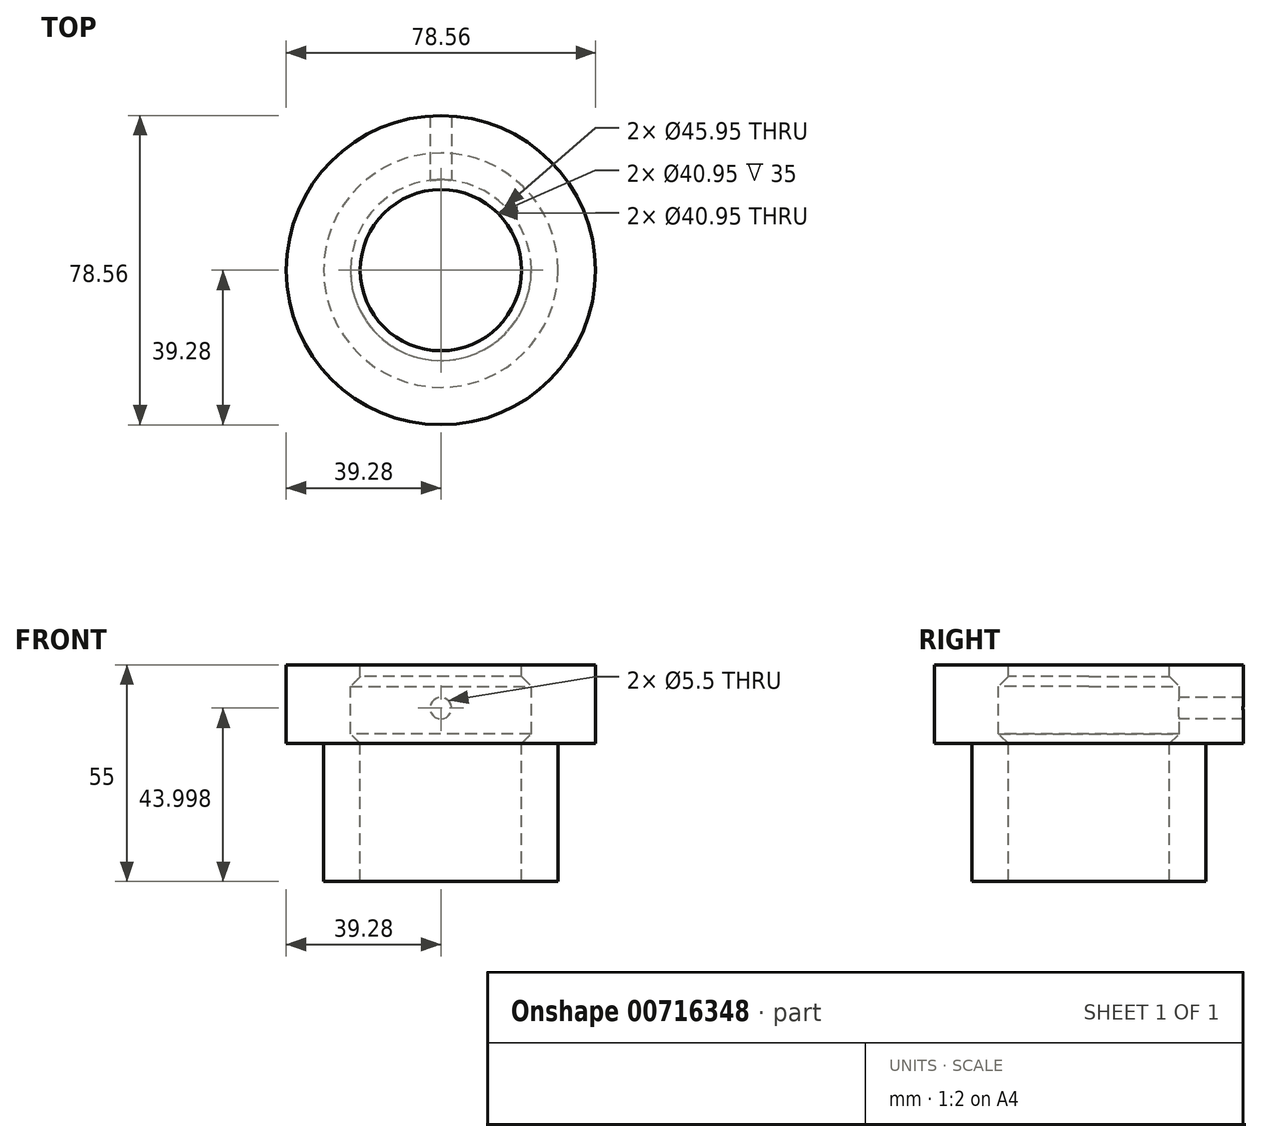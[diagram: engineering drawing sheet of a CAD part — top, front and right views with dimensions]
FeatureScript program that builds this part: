
annotation { "Feature Type Name" : "Feature", "Feature Type Description" : "" }
export const myFeature = defineFeature(function(context is Context, id is Id, definition is map)
    precondition{}
    {
        {
            var Q0;
            Q0=qCreatedBy(makeId("Front.planeOp"),FACE);
            var sketch = newSketch(context, id + "F0", { "sketchPlane" : qUnion([Q0])});
            skLineSegment(sketch, "E0", {"start": v(0, 53.63) * mm, "end": v(0, -51.7) * mm, "construction": true});
            skLineSegment(sketch, "E1", {"start": v(-39.27, 50.83) * mm, "end": v(-39.27, 30.83) * mm});
            skLineSegment(sketch, "E2", {"start": v(-39.27, 30.83) * mm, "end": v(-29.77, 30.83) * mm});
            skLineSegment(sketch, "E3", {"start": v(-29.77, 30.83) * mm, "end": v(-29.77, -4.17) * mm});
            skLineSegment(sketch, "E4", {"start": v(-29.77, -4.17) * mm, "end": v(-20.47, -4.17) * mm});
            skLineSegment(sketch, "E5", {"start": v(-20.47, -4.17) * mm, "end": v(-20.47, 35.83) * mm});
            skLineSegment(sketch, "E6", {"start": v(-20.47, 35.83) * mm, "end": v(-22.97, 35.83) * mm});
            skLineSegment(sketch, "E7", {"start": v(-22.97, 35.83) * mm, "end": v(-22.97, 42.83) * mm});
            skLineSegment(sketch, "E8", {"start": v(-22.97, 42.83) * mm, "end": v(-20.47, 42.83) * mm});
            skLineSegment(sketch, "E9", {"start": v(-20.47, 42.83) * mm, "end": v(-20.47, 50.83) * mm});
            skLineSegment(sketch, "E10", {"start": v(-20.47, 50.83) * mm, "end": v(-39.27, 50.83) * mm});
            skSolve(sketch);
        }
        {
            var Q0;
            Q0=makeQuery(id+"F0.imprint","IMPRINT",FACE,{"disambiguationData":[TD([[makeQuery(id+"F0.imprint","IMPRINT",EDGE,{"derivedFrom":sQuery(id+"F0.wireOp",EDGE,"E1")}),1.0]])]});
            var Q1;
            Q1=sQuery(id+"F0.wireOp",EDGE,"E0");
            revolve(context, id + "F1", {"surfaceOperationType" : NewSurfaceOperationType.NEW, "entities" : qUnion([Q0]), "axis" : qUnion([Q1]), "revolveType" : RevolveType.FULL});
        }
        {
            var Q0;
            Q0=qCreatedBy(makeId("Front.planeOp"),FACE);
            var sketch = newSketch(context, id + "F2", { "sketchPlane" : qUnion([Q0])});
            skPoint(sketch, "E11", {"position": v(0, 39.83) * mm});
            skSolve(sketch);
        }
        {
            var Q0;
            Q0=sQuery(id+"F2.wireOp",VERTEX,"E11");
            var Q1;
            Q1=makeQuery(id+"F1.opRevolve","SWEPT_BODY",BODY,{"disambiguationData":[OSD([sQuery(id+"F0.wireOp",EDGE,"E1"),sQuery(id+"F0.wireOp",EDGE,"E2"),sQuery(id+"F0.wireOp",EDGE,"E3"),sQuery(id+"F0.wireOp",EDGE,"E4"),sQuery(id+"F0.wireOp",EDGE,"E5"),sQuery(id+"F0.wireOp",EDGE,"E6"),sQuery(id+"F0.wireOp",EDGE,"E7"),sQuery(id+"F0.wireOp",EDGE,"E8"),sQuery(id+"F0.wireOp",EDGE,"E9"),sQuery(id+"F0.wireOp",EDGE,"E10")])]});
            hole(context, id + "F3", {"style" : HoleStyle.SIMPLE, "endStyle" : HoleEndStyle.THROUGH, "holeDiameter" : 5.5 * mm, "majorDiameter" : 5 * mm, "isTappedThrough" : true, "tappedDepth" : 12 * mm, "tapClearance" : 3, "locations" : qUnion([Q0]), "scope" : qUnion([Q1])});
        }
        {
            var Q0;
            Q0=makeQuery(id+"F1.opRevolve","SWEPT_EDGE",EDGE,{"disambiguationData":[OSD([sQuery(id+"F0.wireOp",EDGE,"E5"),sQuery(id+"F0.wireOp",EDGE,"E6")])]});
            chamfer(context, id + "F4", {"entities" : qUnion([Q0]), "width" : 5 * mm, "tangentPropagation" : true});
        }
        {
            var Q0;
            Q0=makeQuery(id+"F1.opRevolve","SWEPT_EDGE",EDGE,{"disambiguationData":[OSD([sQuery(id+"F0.wireOp",EDGE,"E8"),sQuery(id+"F0.wireOp",EDGE,"E9")])]});
            chamfer(context, id + "F5", {"entities" : qUnion([Q0]), "width" : 5 * mm, "tangentPropagation" : true});
        }
    });
